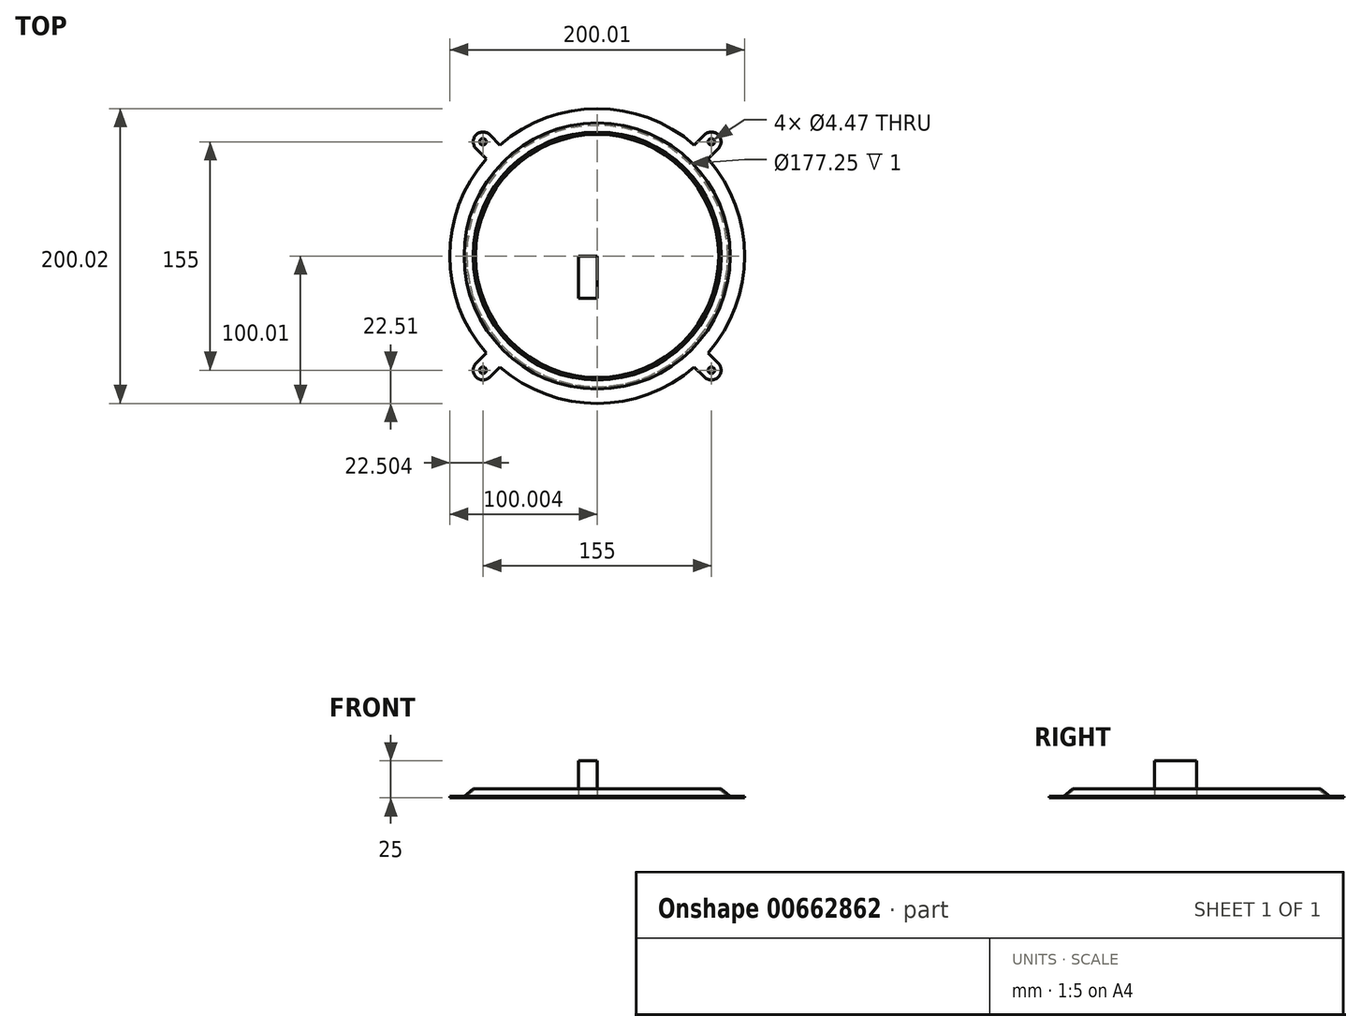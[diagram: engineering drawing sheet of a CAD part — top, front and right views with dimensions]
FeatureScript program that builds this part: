
annotation { "Feature Type Name" : "Feature", "Feature Type Description" : "" }
export const myFeature = defineFeature(function(context is Context, id is Id, definition is map)
    precondition{}
    {
        {
            var Q0;
            Q0=qCreatedBy(makeId("Top.planeOp"),FACE);
            var sketch = newSketch(context, id + "F0", { "sketchPlane" : qUnion([Q0])});
            skArc(sketch, "E0", {"start": v(45.3, -76.74) * mm, "mid": v(19.54, -14) * mm, "end": v(-43.04, 12.16) * mm});
            skArc(sketch, "E1", {"start": v(38.85, -3.64) * mm, "mid": v(38.85, 5.72) * mm, "end": v(29.5, 5.72) * mm});
            skLineSegment(sketch, "E2", {"start": v(29.5, 5.72) * mm, "end": v(22.56, -1.22) * mm});
            skLineSegment(sketch, "E3", {"start": v(38.85, -3.64) * mm, "end": v(31.91, -10.57) * mm});
            skArc(sketch, "E4.trimOffspring", {"start": v(56.68, -76.78) * mm, "mid": v(50.34, -41.42) * mm, "end": v(31.91, -10.57) * mm});
            skLineSegment(sketch, "E5", {"start": v(-43.04, 12.16) * mm, "end": v(-43.01, 21.04) * mm});
            skLineSegment(sketch, "E6", {"start": v(45.3, -76.74) * mm, "end": v(56.68, -76.78) * mm});
            skCircle(sketch, "E7", {"center": v(34.17, 1.04) * mm, "radius": 2.24 * mm});
            skLineSegment(sketch, "E8", {"start": v(-43.01, 21.04) * mm, "end": v(-43, 23.55) * mm});
            skArc(sketch, "E9.trimOffspring", {"start": v(22.56, -1.22) * mm, "mid": v(-7.98, 17.1) * mm, "end": v(-43, 23.55) * mm});
            skLineSegment(sketch, "E10.bottom", {"start": v(-43.33, -76.46) * mm, "end": v(-55.99, -76.46) * mm});
            skLineSegment(sketch, "E10.top", {"start": v(-43.33, -105) * mm, "end": v(-55.99, -105) * mm});
            skLineSegment(sketch, "E10.left", {"start": v(-43.33, -76.46) * mm, "end": v(-43.33, -105) * mm});
            skLineSegment(sketch, "E10.right", {"start": v(-55.99, -76.46) * mm, "end": v(-55.99, -105) * mm});
            skSolve(sketch);
        }
        {
            var Q0;
            Q0=makeQuery(id+"F0.imprint","IMPRINT",FACE,{"disambiguationData":[TD([[makeQuery(id+"F0.imprint","IMPRINT",EDGE,{"derivedFrom":sQuery(id+"F0.wireOp",EDGE,"E0")}),-1.0]])]});
            extrude(context, id + "F1", {"entities" : qUnion([Q0]), "depth" : 1 * mm, "offsetDistance" : 25 * mm});
        }
        {
            var Q0;
            Q0=makeQuery(id+"F0.imprint","IMPRINT",FACE,{"disambiguationData":[TD([[makeQuery(id+"F0.imprint","IMPRINT",EDGE,{"derivedFrom":sQuery(id+"F0.wireOp",EDGE,"E10.bottom")}),1.0]])]});
            extrude(context, id + "F2", {"entities" : qUnion([Q0]), "depth" : 25 * mm, "offsetDistance" : 25 * mm});
        }
        {
            var Q0;
            Q0=makeQuery(id+"F1.opExtrude","SWEPT_BODY",BODY,{"disambiguationData":[OSD([sQuery(id+"F0.wireOp",EDGE,"E0"),sQuery(id+"F0.wireOp",EDGE,"E1"),sQuery(id+"F0.wireOp",EDGE,"E2"),sQuery(id+"F0.wireOp",EDGE,"E3"),sQuery(id+"F0.wireOp",EDGE,"E5"),sQuery(id+"F0.wireOp",EDGE,"E6"),sQuery(id+"F0.wireOp",EDGE,"E7"),sQuery(id+"F0.wireOp",EDGE,"E4.trimOffspring"),sQuery(id+"F0.wireOp",EDGE,"E8"),sQuery(id+"F0.wireOp",EDGE,"E9.trimOffspring")])]});
            var Q1;
            Q1=makeQuery(id+"F2.opExtrude","SWEPT_EDGE",EDGE,{"disambiguationData":[OSD([sQuery(id+"F0.wireOp",EDGE,"E10.bottom"),sQuery(id+"F0.wireOp",EDGE,"E10.left")])]});
            circularPattern(context, id + "F3", {"operationType" : NewBodyOperationType.ADD, "entities" : qUnion([Q0]), "axis" : qUnion([Q1]), "angle" : 360 * degree, "instanceCount" : 4, "equalSpace" : true});
        }
        {
            var Q0;
            Q0=makeQuery(id+"F1.opExtrude","SWEPT_FACE",FACE,{"disambiguationData":[OSD([sQuery(id+"F0.wireOp",EDGE,"E3")])]});
            var sketch = newSketch(context, id + "F4", { "sketchPlane" : qUnion([Q0])});
            skLineSegment(sketch, "E11", {"start": v(15.09, 1) * mm, "end": v(3.63, 1) * mm});
            skLineSegment(sketch, "E12", {"start": v(-2.48, 6) * mm, "end": v(3.63, 1) * mm});
            skPoint(sketch, "E13.orphan", {"position": v(0.67, 1) * mm});
            skLineSegment(sketch, "E14", {"start": v(3.63, 1) * mm, "end": v(5.33, 1) * mm});
            skLineSegment(sketch, "E15", {"start": v(-0.78, 6) * mm, "end": v(5.33, 1) * mm});
            skLineSegment(sketch, "E16", {"start": v(-2.48, 6) * mm, "end": v(-0.78, 6) * mm});
            skSolve(sketch);
        }
        {
            var Q0;
            Q0=makeQuery(id+"F4.imprint","IMPRINT",FACE,{"disambiguationData":[TD([[makeQuery(id+"F4.imprint","IMPRINT",EDGE,{"derivedFrom":sQuery(id+"F4.wireOp",EDGE,"E12")}),1.0]])]});
            var Q1;
            Q1=makeQuery(id+"F2.opExtrude","SWEPT_EDGE",EDGE,{"disambiguationData":[OSD([sQuery(id+"F0.wireOp",EDGE,"E10.bottom"),sQuery(id+"F0.wireOp",EDGE,"E10.left")])]});
            revolve(context, id + "F5", {"operationType" : NewBodyOperationType.ADD, "entities" : qUnion([Q0]), "axis" : qUnion([Q1]), "revolveType" : RevolveType.FULL});
        }
    });
